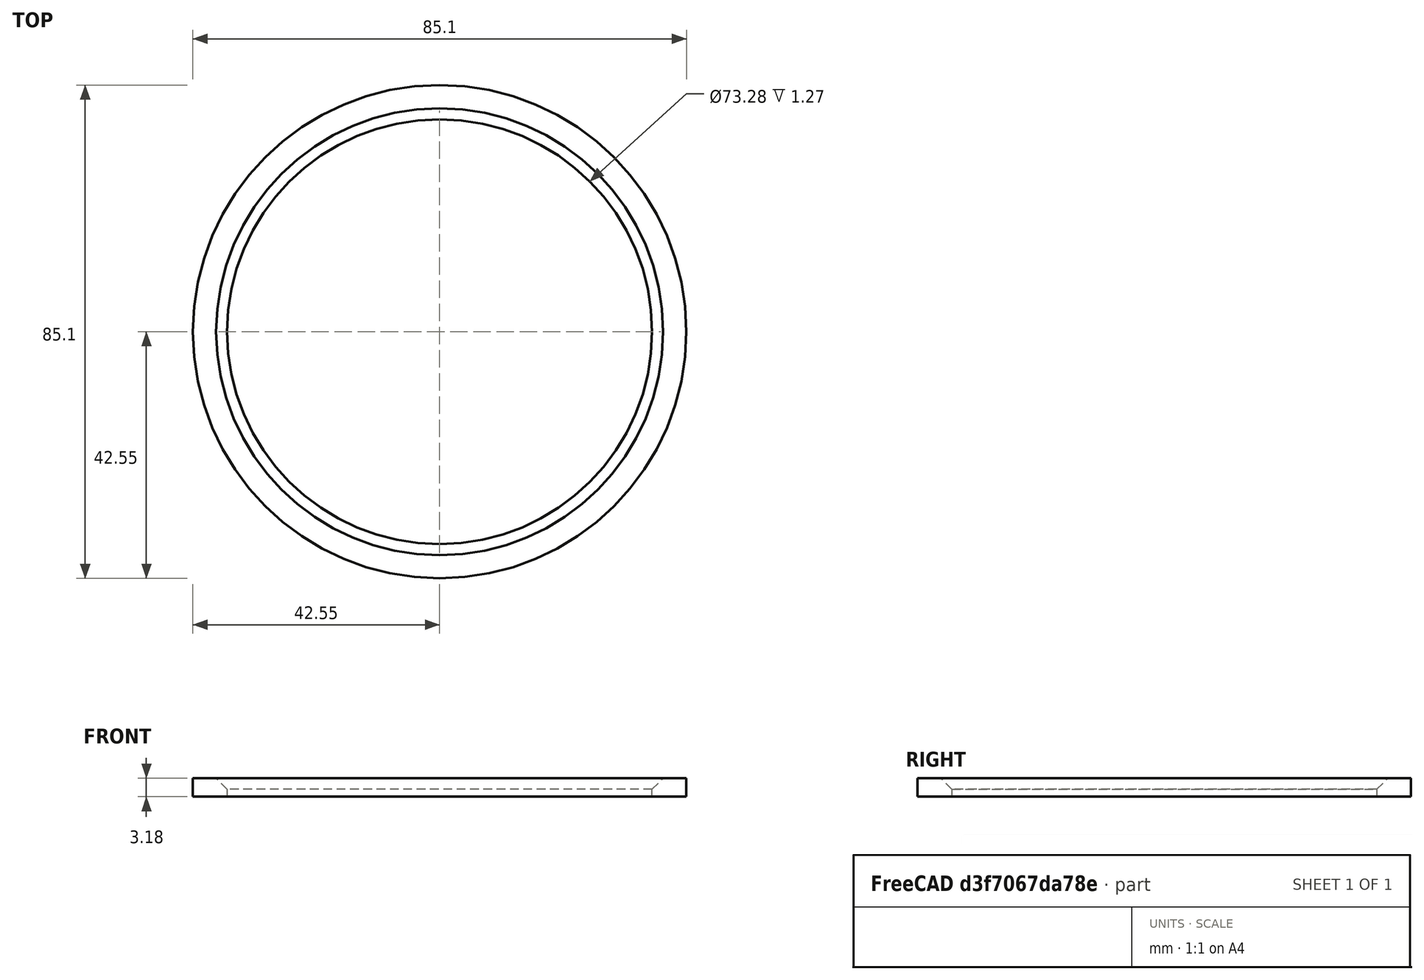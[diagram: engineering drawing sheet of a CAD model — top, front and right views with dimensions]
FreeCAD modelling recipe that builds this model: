
FCSTD DOCUMENT  (FreeCAD 0.19R24291 (Git))
Label: FilterHolderPaperRing
License: All rights reserved
LicenseURL: http://en.wikipedia.org/wiki/All_rights_reserved
objects: Sketcher::SketchObject×1, PartDesign::Pad×1, PartDesign::Chamfer×1, PartDesign::Body×1
note: 6 computed .brp shape members not serialized (recipe doc carries the construction recipe); baked Part::Feature solids carry a one-line shape summary decoded from their .brp

FEATURE [Sketcher::SketchObject] Sketch
  FullyConstrained = true
  MapMode = 5
  Support = -> [XY_Plane]
  sketch-geometry (2):
    g0: Circle CenterX=0 CenterY=0 CenterZ=0 NormalX=0 NormalY=0 NormalZ=1 AngleXU=0 Radius=42.545
    g1: Circle CenterX=0 CenterY=0 CenterZ=0 NormalX=0 NormalY=0 NormalZ=1 AngleXU=0 Radius=36.6395
  constraints (4):
    c: Coincident(g0,g-1)
    c: Coincident(g1,g0)
    c: Radius(g0) = 42.545
    c: Radius(g1) = 36.6395
FEATURE [PartDesign::Pad] Pad
  Direction = (1,1,1)
  Length = 3.175
  Length2 = 100.076
  Profile = -> Sketch
  Type = 0
FEATURE [PartDesign::Chamfer] Chamfer
  Angle = 45
  Base = -> Pad [Edge6]
  BaseFeature = -> Pad
  ChamferType = 0
  FlipDirection = false
  Size = 1.905
  Size2 = 1
  SupportTransform = false
FEATURE [PartDesign::Body] Body
  Group = -> [Sketch,Pad,Chamfer]
  Origin = -> Origin
  Tip = -> Chamfer
